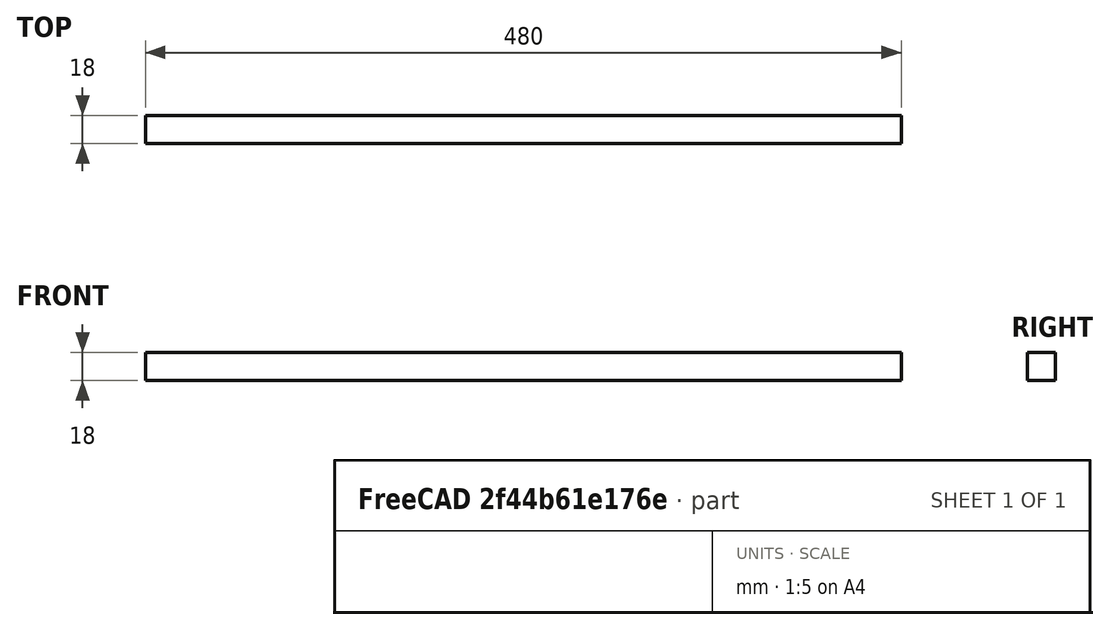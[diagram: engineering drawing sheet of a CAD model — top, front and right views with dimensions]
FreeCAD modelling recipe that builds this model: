
FCSTD DOCUMENT  (FreeCAD 0.20R29177 (Git))
Label: 3000_strut_x_18_18_440
License: All rights reserved
LicenseURL: http://en.wikipedia.org/wiki/All_rights_reserved
objects: Sketcher::SketchObject×1, PartDesign::Pad×1, PartDesign::Body×1
note: 4 computed .brp shape members not serialized (recipe doc carries the construction recipe); baked Part::Feature solids carry a one-line shape summary decoded from their .brp

FEATURE [Sketcher::SketchObject] Sketch
  FullyConstrained = true
  MapMode = 5
  Placement = pos=(0,0,0) rot=(0.57735,0.57735,0.57735;2.0944rad)
  Support = -> [YZ_Plane]
  sketch-geometry (4):
    g0: LineSegment StartX=0 StartY=18 StartZ=0 EndX=18 EndY=18 EndZ=0
    g1: LineSegment StartX=18 StartY=18 StartZ=0 EndX=18 EndY=0 EndZ=0
    g2: LineSegment StartX=18 StartY=0 StartZ=0 EndX=0 EndY=0 EndZ=0
    g3: LineSegment StartX=0 StartY=0 StartZ=0 EndX=0 EndY=18 EndZ=0
  constraints (12):
    c: Coincident(g0,g1)
    c: Coincident(g1,g2)
    c: Coincident(g2,g3)
    c: Coincident(g3,g0)
    c: Horizontal(g0)
    c: Horizontal(g2)
    c: Vertical(g1)
    c: Vertical(g3)
    c: PointOnObject(g0,g-2)
    c: PointOnObject(g1,g-1)
    c: Equal(g1,g0)
    c: DistanceY(g1,g1) = 18
FEATURE [PartDesign::Pad] Pad
  Direction = (1,-2e-16,3e-16)
  Length = 480
  Length2 = 100
  Placement = pos=(0,0,0) rot=(0.57735,0.57735,0.57735;2.0944rad)
  Profile = -> Sketch
  ReferenceAxis = -> Sketch [N_Axis]
  Type = 0
  expr: Length = 480
FEATURE [PartDesign::Body] Body
  Group = -> [Sketch,Pad]
  Origin = -> Origin
  Tip = -> Pad
